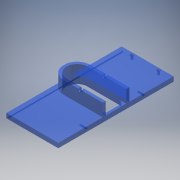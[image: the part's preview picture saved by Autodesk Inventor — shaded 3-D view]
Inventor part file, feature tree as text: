
AUTODESK INVENTOR PART (.ipt)
format: ipt  version: 2018 (Build 220112000, 112)  size: 213,504 bytes
history: native  units: mm
features: extrude x5, mirror x3, hole x3, projected_geometry x1
ambient origin geometry x8: Origin, YZ Plane, XZ Plane, XY Plane, X Axis, Y Axis, Z Axis, Center Point
bodies: Volumenkörper1 (feature_tree)
feature tree (12):
  extrude  "Extrusion1"  Depth=200.0mm
  extrude  "Extrusion2"  Depth=90.0mm
  mirror  "Spiegeln1"
  extrude  "Extrusion3"  Depth=8.0mm TaperAngle=0.0deg
  extrude  "Extrusion4"  Depth=5.0mm
  extrude  "Extrusion5"  Depth=67.5mm
  mirror  "Spiegeln2"
  hole  "Bohrung1"  [1 undecoded]
  mirror  "Spiegeln3"
  hole  "Bohrung2"  [1 undecoded]
  hole  "Bohrung3"  [1 undecoded]
  projected_geometry  "Projizierte Kontur1"
note: 3 required parameter values undecoded (feature->parameter linkage not recoverable at this tier; creation-order binding heuristic only, values carry confidence <= 0.55)
